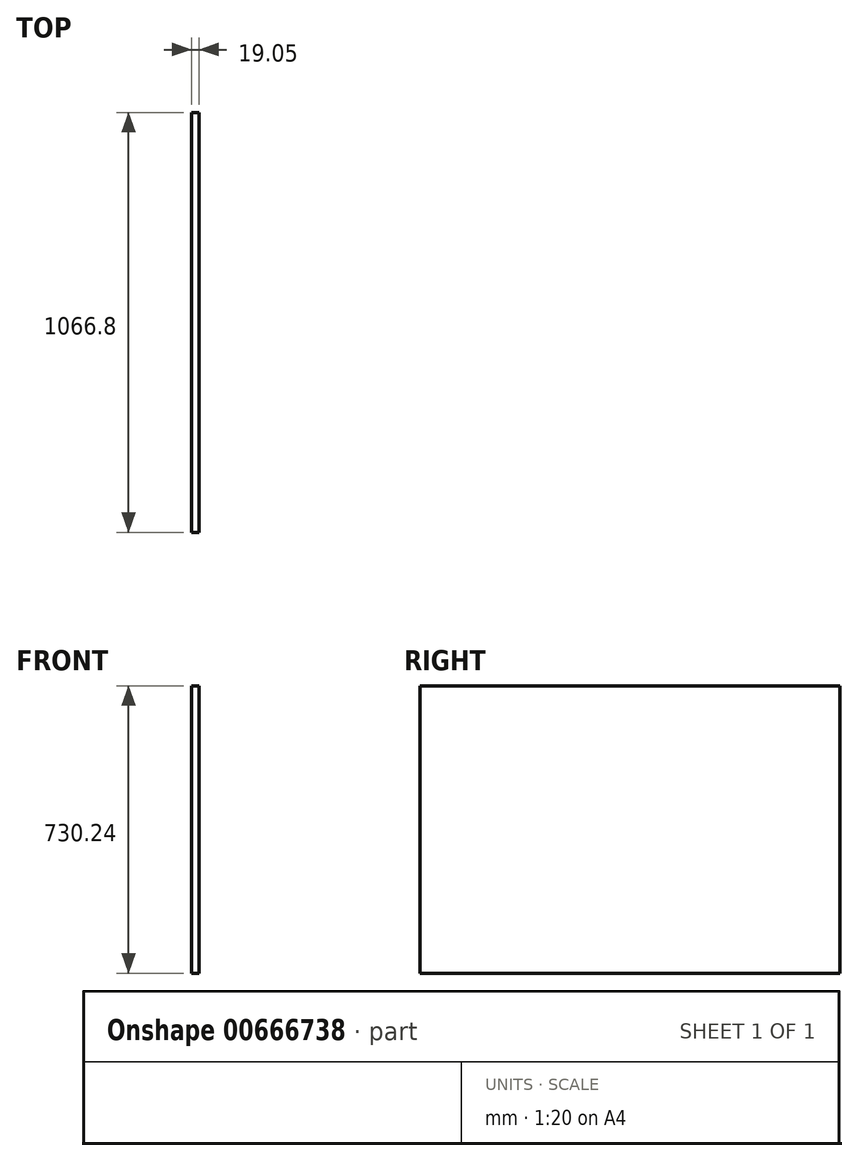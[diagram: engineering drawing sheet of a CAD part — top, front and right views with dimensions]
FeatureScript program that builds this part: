
annotation { "Feature Type Name" : "Feature", "Feature Type Description" : "" }
export const myFeature = defineFeature(function(context is Context, id is Id, definition is map)
    precondition{}
    {
        {
            var Q0;
            Q0=qCreatedBy(makeId("Right.planeOp"),FACE);
            var sketch = newSketch(context, id + "F0", { "sketchPlane" : qUnion([Q0])});
            skLineSegment(sketch, "E0.bottom", {"start": v(533.4, 365.13) * mm, "end": v(-533.4, 365.13) * mm});
            skLineSegment(sketch, "E0.top", {"start": v(533.4, -365.12) * mm, "end": v(-533.4, -365.12) * mm});
            skLineSegment(sketch, "E0.left", {"start": v(533.4, 365.13) * mm, "end": v(533.4, -365.12) * mm});
            skLineSegment(sketch, "E0.right", {"start": v(-533.4, 365.13) * mm, "end": v(-533.4, -365.12) * mm});
            skPoint(sketch, "E0.middle", {"position": v(0, 0) * mm});
            skSolve(sketch);
        }
        {
            var Q0;
            Q0=makeQuery(id+"F0.imprint","IMPRINT",FACE,{"disambiguationData":[TD([[makeQuery(id+"F0.imprint","IMPRINT",EDGE,{"derivedFrom":sQuery(id+"F0.wireOp",EDGE,"E0.bottom")}),1.0]])]});
            extrude(context, id + "F1", {"entities" : qUnion([Q0]), "depth" : 19.05 * mm, "offsetDistance" : 25.4 * mm});
        }
    });
